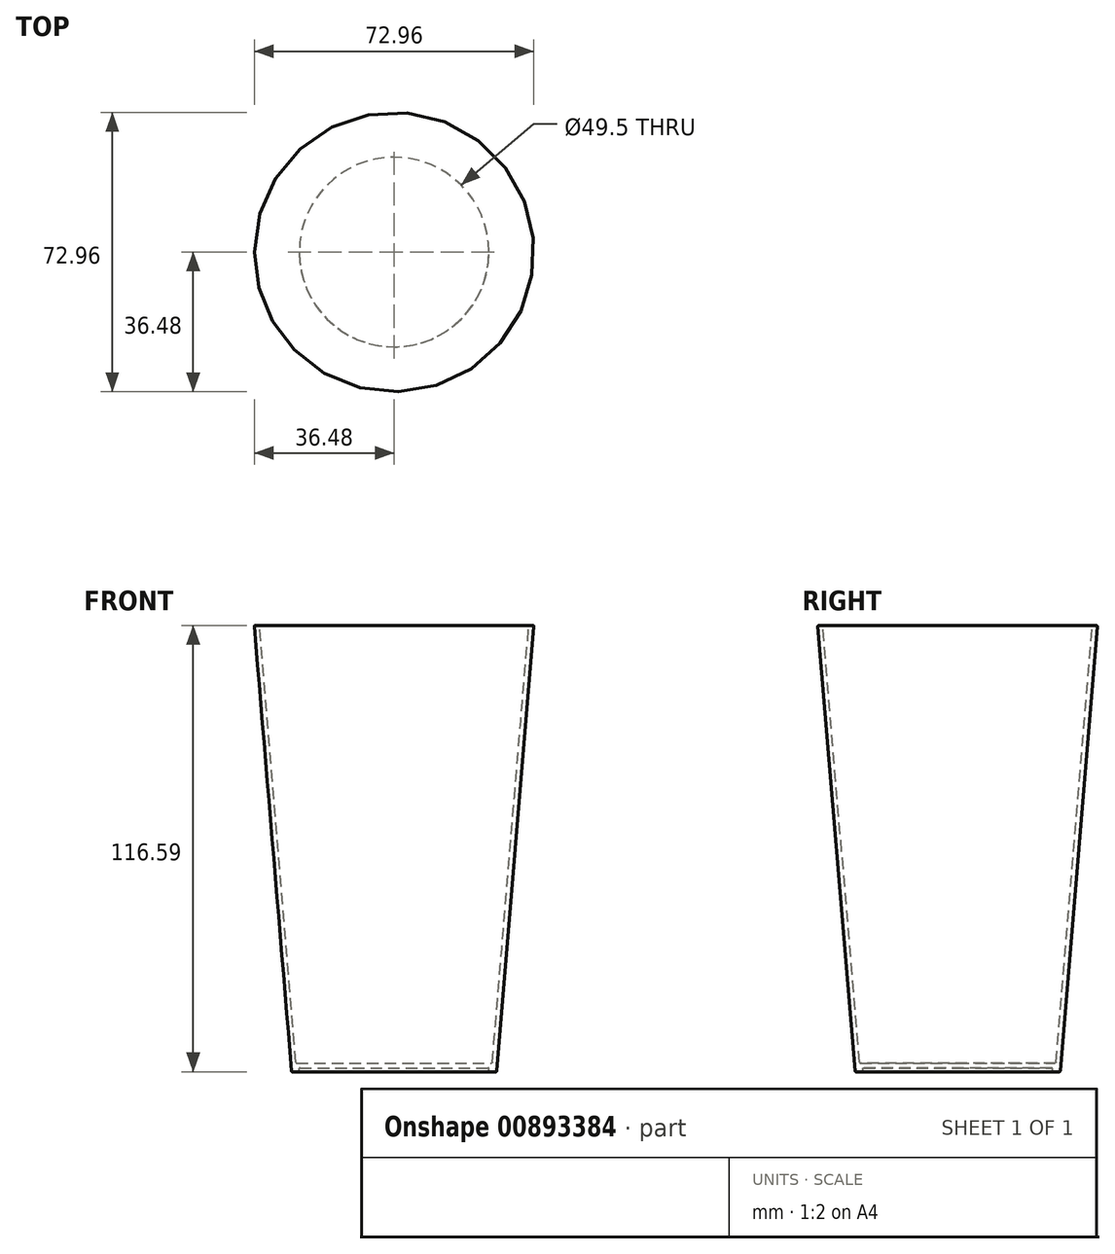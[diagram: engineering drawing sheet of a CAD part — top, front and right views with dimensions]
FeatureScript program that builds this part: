
annotation { "Feature Type Name" : "Feature", "Feature Type Description" : "" }
export const myFeature = defineFeature(function(context is Context, id is Id, definition is map)
    precondition{}
    {
        {
            var Q0;
            Q0=qCreatedBy(makeId("Front.planeOp"),FACE);
            var sketch = newSketch(context, id + "F0", { "sketchPlane" : qUnion([Q0])});
            skLineSegment(sketch, "E0", {"start": v(-24.75, 0) * mm, "end": v(0, 0) * mm});
            skLineSegment(sketch, "E1", {"start": v(-24.75, 0) * mm, "end": v(-24.75, -1) * mm});
            skLineSegment(sketch, "E2", {"start": v(-24.75, -1) * mm, "end": v(-26.75, -1) * mm});
            skLineSegment(sketch, "E3", {"start": v(-26.75, -1) * mm, "end": v(-36.5, 115.5) * mm});
            skLineSegment(sketch, "E4", {"start": v(-36.5, 115.5) * mm, "end": v(-35.2, 115.6) * mm});
            skLineSegment(sketch, "E5", {"start": v(-35.2, 115.6) * mm, "end": v(-25.64, 1.3) * mm});
            skLineSegment(sketch, "E6", {"start": v(-25.64, 1.3) * mm, "end": v(0, 1.3) * mm});
            skLineSegment(sketch, "E7", {"start": v(0, 1.3) * mm, "end": v(0, 0) * mm});
            skSolve(sketch);
        }
        {
            var Q0;
            Q0=makeQuery(id+"F0.imprint","IMPRINT",FACE,{"disambiguationData":[TD([[makeQuery(id+"F0.imprint","IMPRINT",EDGE,{"derivedFrom":sQuery(id+"F0.wireOp",EDGE,"E0")}),1.0]])]});
            var Q1;
            Q1=sQuery(id+"F0.wireOp",EDGE,"E7");
            revolve(context, id + "F1", {"surfaceOperationType" : NewSurfaceOperationType.NEW, "entities" : qUnion([Q0]), "axis" : qUnion([Q1]), "revolveType" : RevolveType.FULL});
        }
        {
            var Q0;
            Q0=makeQuery(id+"F1.opRevolve","SWEPT_EDGE",EDGE,{"disambiguationData":[OSD([sQuery(id+"F0.wireOp",EDGE,"E3"),sQuery(id+"F0.wireOp",EDGE,"E4")])]});
            var Q1;
            Q1=makeQuery(id+"F1.opRevolve","SWEPT_EDGE",EDGE,{"disambiguationData":[OSD([sQuery(id+"F0.wireOp",EDGE,"E4"),sQuery(id+"F0.wireOp",EDGE,"E5")])]});
            var Q2;
            Q2=makeQuery(id+"F1.opRevolve","SWEPT_EDGE",EDGE,{"disambiguationData":[OSD([sQuery(id+"F0.wireOp",EDGE,"E0"),sQuery(id+"F0.wireOp",EDGE,"E1")])]});
            var Q3;
            Q3=makeQuery(id+"F1.opRevolve","SWEPT_EDGE",EDGE,{"disambiguationData":[OSD([sQuery(id+"F0.wireOp",EDGE,"E1"),sQuery(id+"F0.wireOp",EDGE,"E2")])]});
            var Q4;
            Q4=makeQuery(id+"F1.opRevolve","SWEPT_EDGE",EDGE,{"disambiguationData":[OSD([sQuery(id+"F0.wireOp",EDGE,"E2"),sQuery(id+"F0.wireOp",EDGE,"E3")])]});
            var Q5;
            Q5=makeQuery(id+"F1.opRevolve","SWEPT_EDGE",EDGE,{"disambiguationData":[OSD([sQuery(id+"F0.wireOp",EDGE,"E5"),sQuery(id+"F0.wireOp",EDGE,"E6")])]});
            fillet(context, id + "F2", {"entities" : qUnion([Q0, Q1, Q2, Q3, Q4, Q5]), "radius" : 0.2 * mm, "tangentPropagation" : true, "allowEdgeOverflow" : false});
        }
    });
